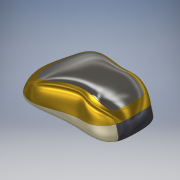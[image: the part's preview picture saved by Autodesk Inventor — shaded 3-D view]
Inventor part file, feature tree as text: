
AUTODESK INVENTOR PART (.ipt)
format: ipt  version: 2018 (Build 220112000, 112)  size: 7,019,520 bytes
history: native  units: in
note: dims shown in document units (in); Inventor stores cm internally (conversion verified against a paired STEP export)
features: other x8, split x3, shell x1, sketch x1
ambient origin geometry x8: Origin, YZ Plane, XZ Plane, XY Plane, X Axis, Y Axis, Z Axis, Center Point
bodies: Solid6 (feature_tree), Solid9 (feature_tree), Solid10 (feature_tree), Solid11 (feature_tree), Solid12 (feature_tree), Solid13 (feature_tree), Solid14 (feature_tree)
feature tree (13):
  other  "Top"
  other  "Side"
  other  "Form6"
  shell  "Shell1"  Thickness=3.0in
  split  "Split2"
  split  "Split3"
  split  "Split4"
  other  "Lip4"
  other  "Lip5"
  other  "Lip6"
  other  "Image3"
  other  "Image4"
  sketch  "Sketch4"  dims[d104=3.0in d111=0.1in d119=2.25in d120=1.5in d121=0.0479in d122=0.25in d145=0.03in d146=0.03in d147=0.0in d148=0.0in d149=0.0in d150=0.0in d151=0.03in d152=0.03in d153=0.0in d154=0.0in d155=0.0in d156=0.0in d157=0.03in d158=0.03in d159=0.0in d160=0.0in d161=0.0in d162=0.0in]
